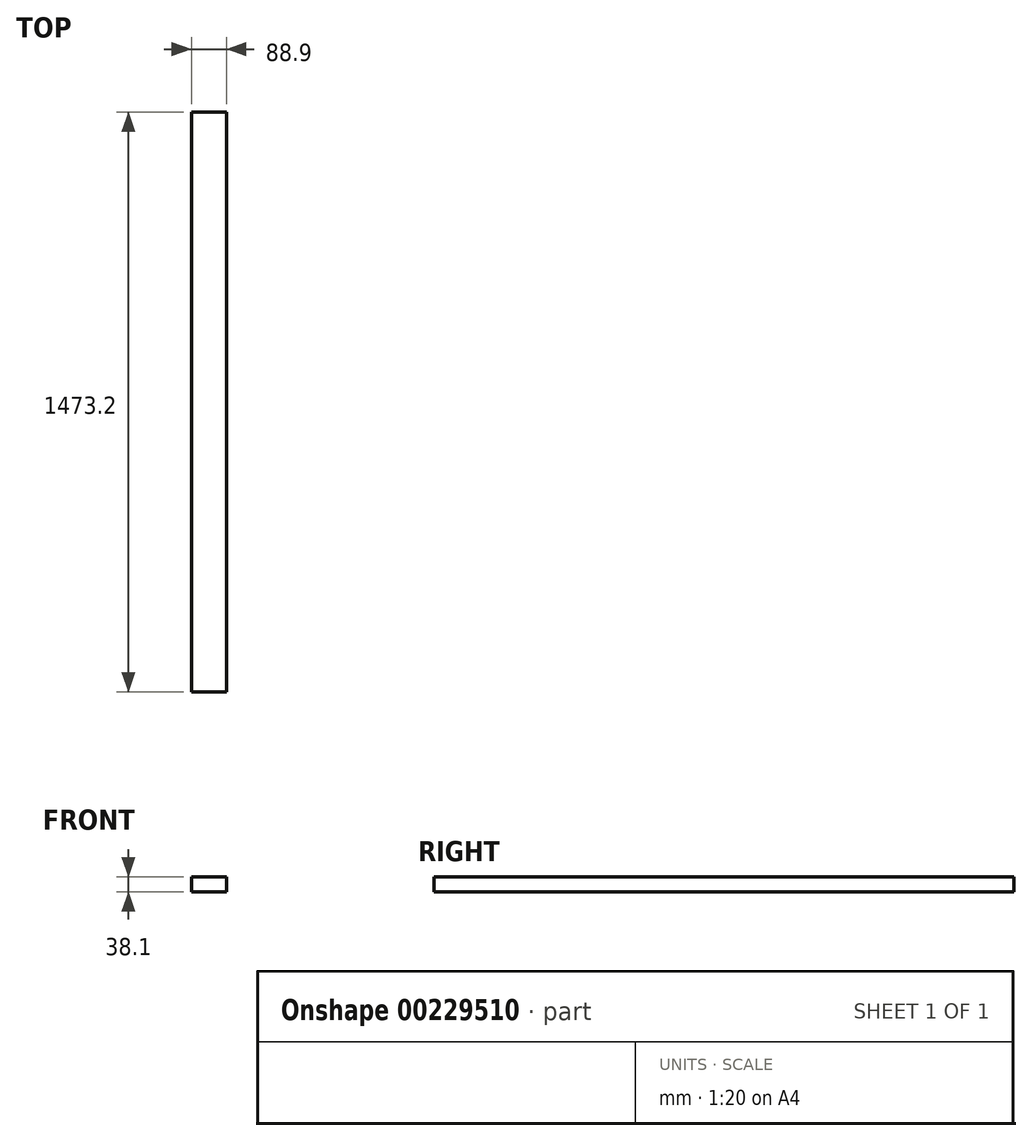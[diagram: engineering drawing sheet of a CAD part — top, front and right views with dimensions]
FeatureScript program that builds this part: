
annotation { "Feature Type Name" : "Feature", "Feature Type Description" : "" }
export const myFeature = defineFeature(function(context is Context, id is Id, definition is map)
    precondition{}
    {
        {
            var Q0;
            Q0=qCreatedBy(makeId("Front.planeOp"),FACE);
            var sketch = newSketch(context, id + "F0", { "sketchPlane" : qUnion([Q0])});
            skLineSegment(sketch, "E0.bottom", {"start": v(0, 0) * mm, "end": v(88.9, 0) * mm});
            skLineSegment(sketch, "E0.top", {"start": v(0, -38.1) * mm, "end": v(88.9, -38.1) * mm});
            skLineSegment(sketch, "E0.left", {"start": v(0, 0) * mm, "end": v(0, -38.1) * mm});
            skLineSegment(sketch, "E0.right", {"start": v(88.9, 0) * mm, "end": v(88.9, -38.1) * mm});
            skSolve(sketch);
        }
        {
            var Q0;
            Q0=qSketchRegion(id+"F0",true);
            extrude(context, id + "F1", {"entities" : qUnion([Q0]), "depth" : 1473.2 * mm});
        }
    });
